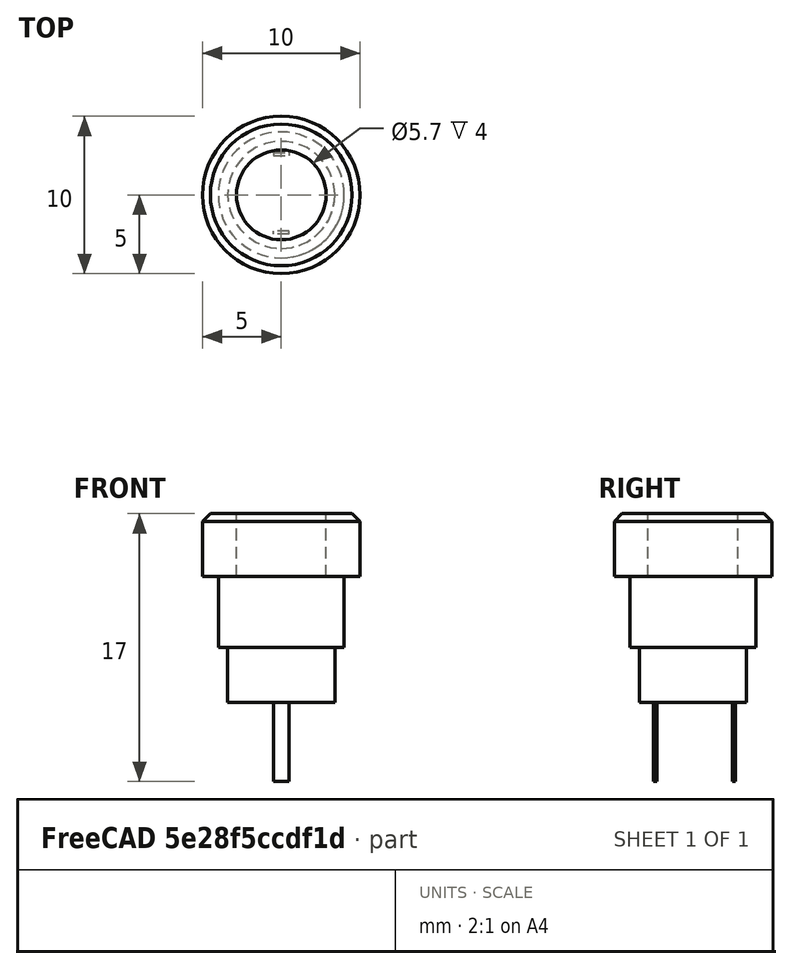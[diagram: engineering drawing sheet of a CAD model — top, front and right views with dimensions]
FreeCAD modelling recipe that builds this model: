
FCSTD DOCUMENT
Label: power_connector_5_5_x_2_1
License: CC-BY 3.0
LicenseURL: http://creativecommons.org/licenses/by/3.0/
objects: Part::Cylinder×4, Part::Box×2, Part::Chamfer×1, Part::MultiFuse×1, Part::Cut×1
note: 9 computed .brp shape members not serialized (recipe doc carries the construction recipe); baked Part::Feature solids carry a one-line shape summary decoded from their .brp

FEATURE [Part::Cylinder] Cylinder001  label="Body"
  Angle = 360
  Height = 4.6
  Placement = pos=(0,0,-4.5) rot=(0,0,1;0rad)
  Radius = 4
FEATURE [Part::Box] Box  label="contact01"
  Height = 5.1
  Length = 1
  Placement = pos=(-0.5,2.5,-13) rot=(0,0,1;0rad)
  Width = 0.2
FEATURE [Part::Cylinder] Cylinder002
  Angle = 360
  Height = 8.5
  Placement = pos=(0,0,-8) rot=(0,0,1;0rad)
  Radius = 3.4
FEATURE [Part::Box] Box001  label="contact002"
  Height = 5.1
  Length = 1
  Placement = pos=(-0.5,-2.5,-13) rot=(0,0,1;0rad)
  Width = 0.2
FEATURE [Part::Cylinder] Cylinder  label="Bezel"
  Angle = 360
  Height = 4
  Radius = 5
FEATURE [Part::Chamfer] Chamfer
  Base = -> Cylinder
  Edges = 1 edges r=0.5: [Edge1]
FEATURE [Part::MultiFuse] Fusion  label="power_connector_blank"
  Shapes = -> [Cylinder001,Box,Cylinder002,Box001,Chamfer]
FEATURE [Part::Cylinder] Cylinder003  label="hole"
  Angle = 360
  Height = 10
  Radius = 2.85
FEATURE [Part::Cut] Cut  label="PowerConnector"
  Base = -> Fusion
  Tool = -> Cylinder003
